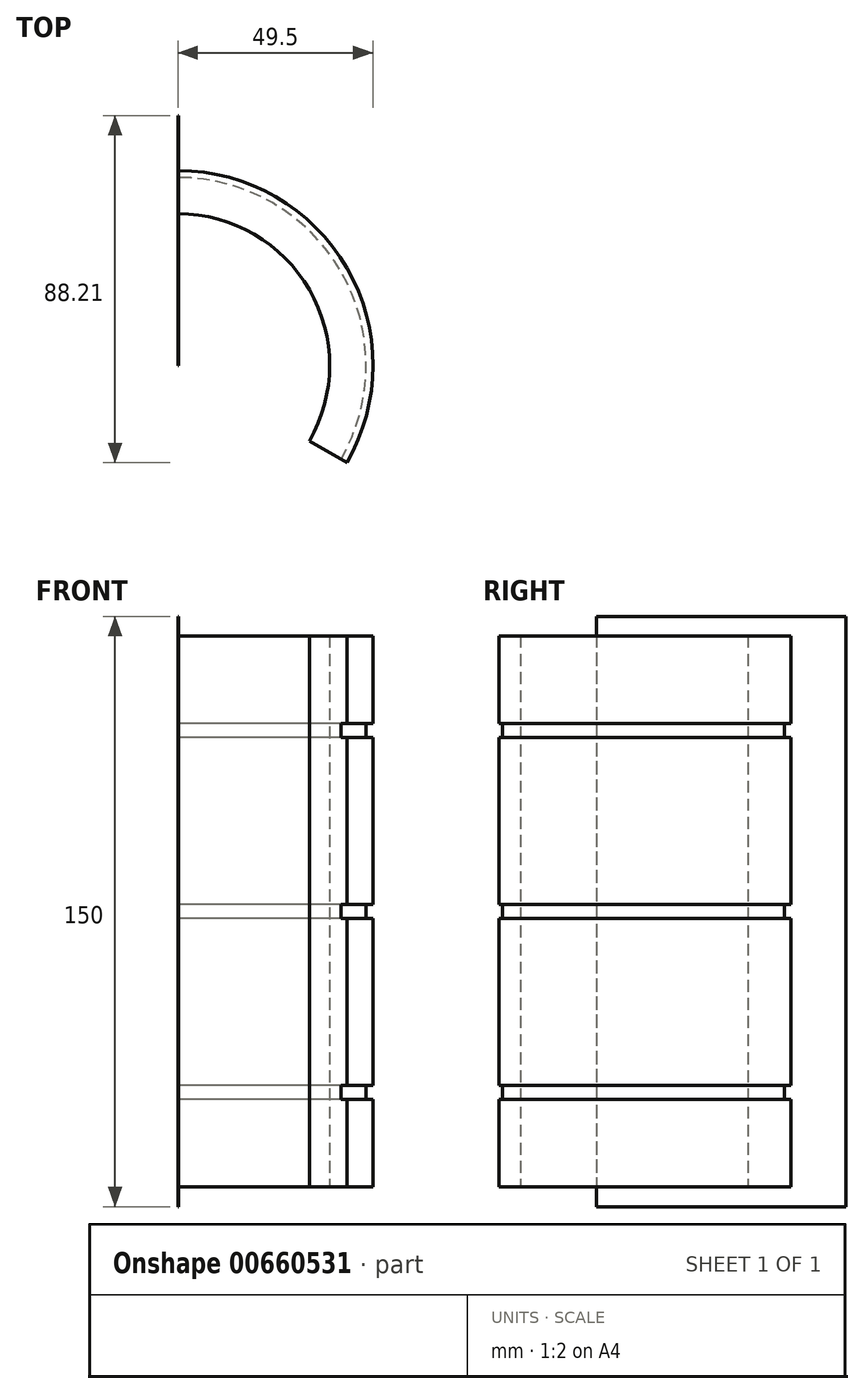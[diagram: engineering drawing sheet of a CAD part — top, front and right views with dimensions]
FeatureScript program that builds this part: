
annotation { "Feature Type Name" : "Feature", "Feature Type Description" : "" }
export const myFeature = defineFeature(function(context is Context, id is Id, definition is map)
    precondition{}
    {
        {
            var Q0;
            Q0=qCreatedBy(makeId("Top.planeOp"),FACE);
            var sketch = newSketch(context, id + "F0", { "sketchPlane" : qUnion([Q0])});
            skCircle(sketch, "E0", {"center": v(0, 0) * mm, "radius": 38.5 * mm});
            skCircle(sketch, "E1", {"center": v(0, 0) * mm, "radius": 49.5 * mm});
            skSolve(sketch);
        }
        {
            var Q0;
            Q0=makeQuery(id+"F0.imprint","IMPRINT",FACE,{"disambiguationData":[TD([[makeQuery(id+"F0.imprint","IMPRINT",EDGE,{"derivedFrom":sQuery(id+"F0.wireOp",EDGE,"E0")}),-1.0]])]});
            extrude(context, id + "F1", {"entities" : qUnion([Q0]), "endBound" : BoundingType.SYMMETRIC, "depth" : 140 * mm, "offsetDistance" : 25 * mm});
        }
        {
            var Q0;
            Q0=qCreatedBy(makeId("Top.planeOp"),FACE);
            var sketch = newSketch(context, id + "F2", { "sketchPlane" : qUnion([Q0])});
            skCircle(sketch, "E2", {"center": v(0, 0) * mm, "radius": 54.33 * mm});
            skCircle(sketch, "E3", {"center": v(0, 0) * mm, "radius": 47.75 * mm});
            skSolve(sketch);
        }
        {
            var Q0;
            Q0=makeQuery(id+"F2.imprint","IMPRINT",FACE,{"disambiguationData":[TD([[makeQuery(id+"F2.imprint","IMPRINT",EDGE,{"derivedFrom":sQuery(id+"F2.wireOp",EDGE,"E2")}),1.0]])]});
            extrude(context, id + "F3", {"entities" : qUnion([Q0]), "operationType" : NewBodyOperationType.REMOVE, "endBound" : BoundingType.SYMMETRIC, "depth" : 3.5 * mm, "offsetDistance" : 25 * mm});
        }
        {
            var Q0;
            Q0=qCreatedBy(makeId("Top.planeOp"),FACE);
            cPlane(context, id + "F4", {"entities" : qUnion([Q0]), "cplaneType" : CPlaneType.OFFSET, "offset" : 46 * mm, "width" : 150 * mm, "height" : 150 * mm});
        }
        {
            var Q0;
            Q0=qCreatedBy(makeId("Top.planeOp"),FACE);
            cPlane(context, id + "F5", {"entities" : qUnion([Q0]), "cplaneType" : CPlaneType.OFFSET, "offset" : 46 * mm, "oppositeDirection" : true, "width" : 150 * mm, "height" : 150 * mm});
        }
        {
            var Q0;
            Q0=qCreatedBy(id+"F4.planeOp",FACE);
            var sketch = newSketch(context, id + "F6", { "sketchPlane" : qUnion([Q0])});
            skCircle(sketch, "E4", {"center": v(0, 0) * mm, "radius": 54.33 * mm});
            skCircle(sketch, "E5", {"center": v(0, 0) * mm, "radius": 47.75 * mm});
            skSolve(sketch);
        }
        {
            var Q0;
            Q0=qCreatedBy(id+"F5.planeOp",FACE);
            var sketch = newSketch(context, id + "F7", { "sketchPlane" : qUnion([Q0])});
            skCircle(sketch, "E6", {"center": v(0, 0) * mm, "radius": 54.33 * mm});
            skCircle(sketch, "E7", {"center": v(0, 0) * mm, "radius": 47.75 * mm});
            skSolve(sketch);
        }
        {
            var Q0;
            Q0=makeQuery(id+"F6.imprint","IMPRINT",FACE,{"disambiguationData":[TD([[makeQuery(id+"F6.imprint","IMPRINT",EDGE,{"derivedFrom":sQuery(id+"F6.wireOp",EDGE,"E4")}),1.0]])]});
            extrude(context, id + "F8", {"entities" : qUnion([Q0]), "operationType" : NewBodyOperationType.REMOVE, "endBound" : BoundingType.SYMMETRIC, "depth" : 3.5 * mm, "offsetDistance" : 25 * mm});
        }
        {
            var Q0;
            Q0=makeQuery(id+"F7.imprint","IMPRINT",FACE,{"disambiguationData":[TD([[makeQuery(id+"F7.imprint","IMPRINT",EDGE,{"derivedFrom":sQuery(id+"F7.wireOp",EDGE,"E6")}),1.0]])]});
            extrude(context, id + "F9", {"entities" : qUnion([Q0]), "operationType" : NewBodyOperationType.REMOVE, "endBound" : BoundingType.SYMMETRIC, "depth" : 3.5 * mm, "offsetDistance" : 25 * mm});
        }
        {
            var Q0;
            Q0=qCreatedBy(makeId("Top.planeOp"),FACE);
            var sketch = newSketch(context, id + "F10", { "sketchPlane" : qUnion([Q0])});
            skLineSegment(sketch, "E8", {"start": v(0, 0) * mm, "end": v(0, 63.46) * mm});
            skLineSegment(sketch, "E9", {"start": v(0, 63.46) * mm, "end": v(0.1, 63.46) * mm});
            skLineSegment(sketch, "E10", {"start": v(0, 0) * mm, "end": v(0.1, 0) * mm});
            skLineSegment(sketch, "E11", {"start": v(0.1, 63.46) * mm, "end": v(0.1, 0) * mm});
            skPoint(sketch, "E12.orphan", {"position": v(16.09, 0) * mm});
            skSolve(sketch);
        }
        {
            var Q0;
            Q0=qCreatedBy(makeId("Front.planeOp"),FACE);
            var sketch = newSketch(context, id + "F11", { "sketchPlane" : qUnion([Q0])});
            skLineSegment(sketch, "E13", {"start": v(0, 0) * mm, "end": v(0, 96.78) * mm});
            skLineSegment(sketch, "E14", {"start": v(0, 96.78) * mm, "end": v(0, -96.84) * mm});
            skSolve(sketch);
        }
        {
            var Q0;
            Q0=makeQuery(id+"F10.imprint","IMPRINT",FACE,{"disambiguationData":[TD([[makeQuery(id+"F10.imprint","IMPRINT",EDGE,{"derivedFrom":sQuery(id+"F10.wireOp",EDGE,"E8")}),-1.0]])]});
            extrude(context, id + "F12", {"entities" : qUnion([Q0]), "operationType" : NewBodyOperationType.ADD, "endBound" : BoundingType.SYMMETRIC, "depth" : 150 * mm, "offsetDistance" : 25 * mm});
        }
        {
            var Q0;
            Q0=makeQuery(id+"F12.opExtrude","SWEPT_FACE",FACE,{"disambiguationData":[OSD([sQuery(id+"F10.wireOp",EDGE,"E8")])]});
            var Q1;
            Q1=sQuery(id+"F11.wireOp",EDGE,"E14");
            revolve(context, id + "F13", {"entities" : qUnion([Q0]), "axis" : qUnion([Q1]), "revolveType" : RevolveType.ONE_DIRECTION, "oppositeDirection" : true, "angle" : 240 * degree});
        }
        {
            var Q0;
            {var subQ0=sQuery(id+"F10.wireOp",EDGE,"E8");Q0=makeQuery(id+"F13.opRevolve","SWEPT_FACE",FACE,{"disambiguationData":[OSD([subQ0]),TDD([makeQuery(id+"F12.opExtrude","CAP_EDGE",EDGE,{"disambiguationData":[OSD([subQ0])],"isStart":false})])]});}
            extrude(context, id + "F14", {"entities" : qUnion([Q0]), "operationType" : NewBodyOperationType.REMOVE, "oppositeDirection" : true, "depth" : 150 * mm, "offsetDistance" : 25 * mm});
        }
    });
